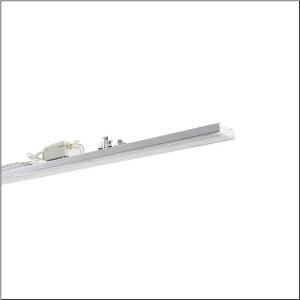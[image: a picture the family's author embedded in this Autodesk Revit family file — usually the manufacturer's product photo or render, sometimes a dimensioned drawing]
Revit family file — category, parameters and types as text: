
# Revit family: licross_r__21_recessed_mo_52te1ecn485g_1eda
name_source: partatom
category: Lighting Fixtures
units: mm (PartAtom-declared; Revit-internal decimal feet)

## family parameters
Cut with Voids When Loaded = No
Host = Face
Light Source = No
Part Type = Normal
Room Calculation Point = No
Round Connector Dimension = Use Diameter
Shared = No

## types (1)
- --- (1 x LED, 8960 lm, 49.9 W, 4000K)
    Apparent Load = 50 VA
    CIE Flux Codes = 85 95 99 100 100
    Color Rendering = 80
    Color Temperature = 4000K
    Default Elevation = 1800 mm
    Description = Licross® 21 Recessed MO, luminaire insert, of sheet steel, galvanised, coil coated, white, length: 1.500mm, width: 66mm, height: 67mm, LED rated luminous flux: 8.960lm, light colour: 840, control gear: ON/OFF Multilumen, CLOi, control gear: ECG Multilumen, with plug, 3-pole, with phase selection, mains connection: 220..240V, AC, 50/60Hz, start of lifetime: 50W, end of service life: 61W, halogen-free wiring, primary light control with lens, of plastic, primary optical cover: cover, of PMMA, light emission: direct distribution, primary light characteristic: symmetric, protection rating (complete): IP54, insulation class (complete): insulation class I (protective earthing), certification: CE, ENEC, VDE, UKCA, protection symbol: D if used in an environment with non-conductive dust loads with corresponding accessories, impact resistance: IK06, permissible ambient temperature for indoor applications: -35..+40°C, corresponds to IFS (International Featured Standards) requirements for safety and quality in the food industry, reducing of maximum allowable ambient temperature of 5°C with ceiling mounting, LABS conformity tested according to VDMA 24364:2018-05, packaging unit: 1 piece
    Height = 58 mm
    Lamp = 1 x LED
    Lamp Light Flux = 8960 lm
    Lamp Power = 49.9 W
    Lamp count = 1
    Length = 1500 mm
    Luminous efficacy = 180 lm/W
    Manufacturer = Siteco
    ModVariant = No
    Model = 52TE1ECN485G
    Mounting Place = Ceiling
    Mounting Type = Pendant
    Number of Poles = 1
    OnlyDefault = Yes
    Power Factor = 1
    Product Name = Licross® 21 Recessed MO
    Product group = luminaire insert
    ProductGroupID = 901
    Protection Class = Protection class I
    Protection Degree = IP 54
    RLX_Detail_Level = 1
    RLX_Emergency_Light_Flux = 0 lm
    RLX_Emergency_Type = 0
    RLX_Emergency_Type_DB = No
    RlxData = <blob elided: 22417 chars, md5=0a950fe2>
    Socket = socket
    Standby Power = 0 W
    System Light Flux = 8960 lm
    System Power = 50 W
    Type Comments = factory setting: luminous flux: 100 % | (A | C | E) | 116 mA
    Type Image = l_1296930.jpg
    URL = http://relux.com
    VarID = @adj_040017
    Voltage = 0 V
    Weight = 0.00 kg
    Width = 66 mm

## geometry (parser evidence)
native form markers: Blend x4, Sweep x10
no freeform markers — native parametric forms only
